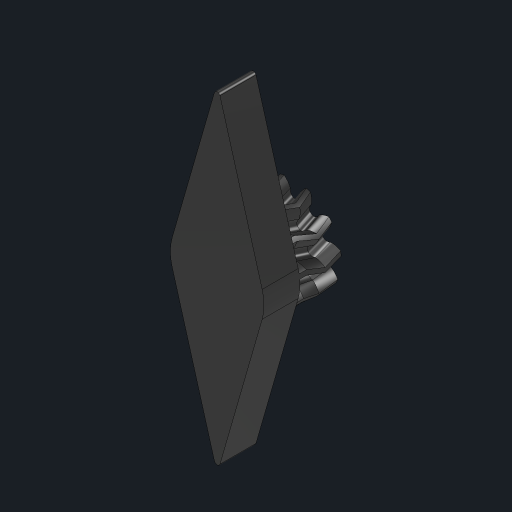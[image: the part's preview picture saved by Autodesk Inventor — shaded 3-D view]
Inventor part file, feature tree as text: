
AUTODESK INVENTOR PART (.ipt)
format: ipt  version: 2023.2 (Build 272271030, 271C)  size: 5,975,552 bytes
history: native  units: mm
features: sketch x4, extrude x4, projected_geometry x3, helix x1, pattern_circular x1, mirror x1, fillet x1
ambient origin geometry x8: Origin, YZ Plane, XZ Plane, XY Plane, X Axis, Y Axis, Z Axis, Center Point
bodies: Solid1 (feature_tree)
feature tree (15):
  sketch  "Sketch1"  dims[d0=2.5mm d1=0.0mm]
  extrude  "Extrusion1"  Depth=10.0mm TaperAngle=0.0deg
  helix  "Coil1"  [1 undecoded]
  pattern_circular  "Circular Pattern1"  [2 undecoded]
  mirror  "Mirror1"
  extrude  "Extrusion2"  [1 undecoded]
  extrude  "Extrusion3"  [1 undecoded]
  fillet  "Fillet1"  [1 undecoded]
  extrude  "Extrusion4"  [1 undecoded]
  sketch  "Sketch2"  dims[d2=110.1mm d3=10.0mm d4=10.0mm d5=0.0mm d6=90.0deg d7=90.0deg d8=0.0mm d9=0.0mm d10=110.0mm d11=360.0deg d13=1.0mm d14=0.0mm d15=47.0mm]
  projected_geometry  "Projected Loop1"
  sketch  "Sketch3"  dims[d16=5.0mm d17=0.0mm]
  projected_geometry  "Projected Loop2"
  sketch  "Sketch4"  dims[d18=0.4mm d19=0.25mm d20=0.0mm]
  projected_geometry  "Projected Loop3"
note: 7 required parameter values undecoded (feature->parameter linkage not recoverable at this tier; creation-order binding heuristic only, values carry confidence <= 0.55)
